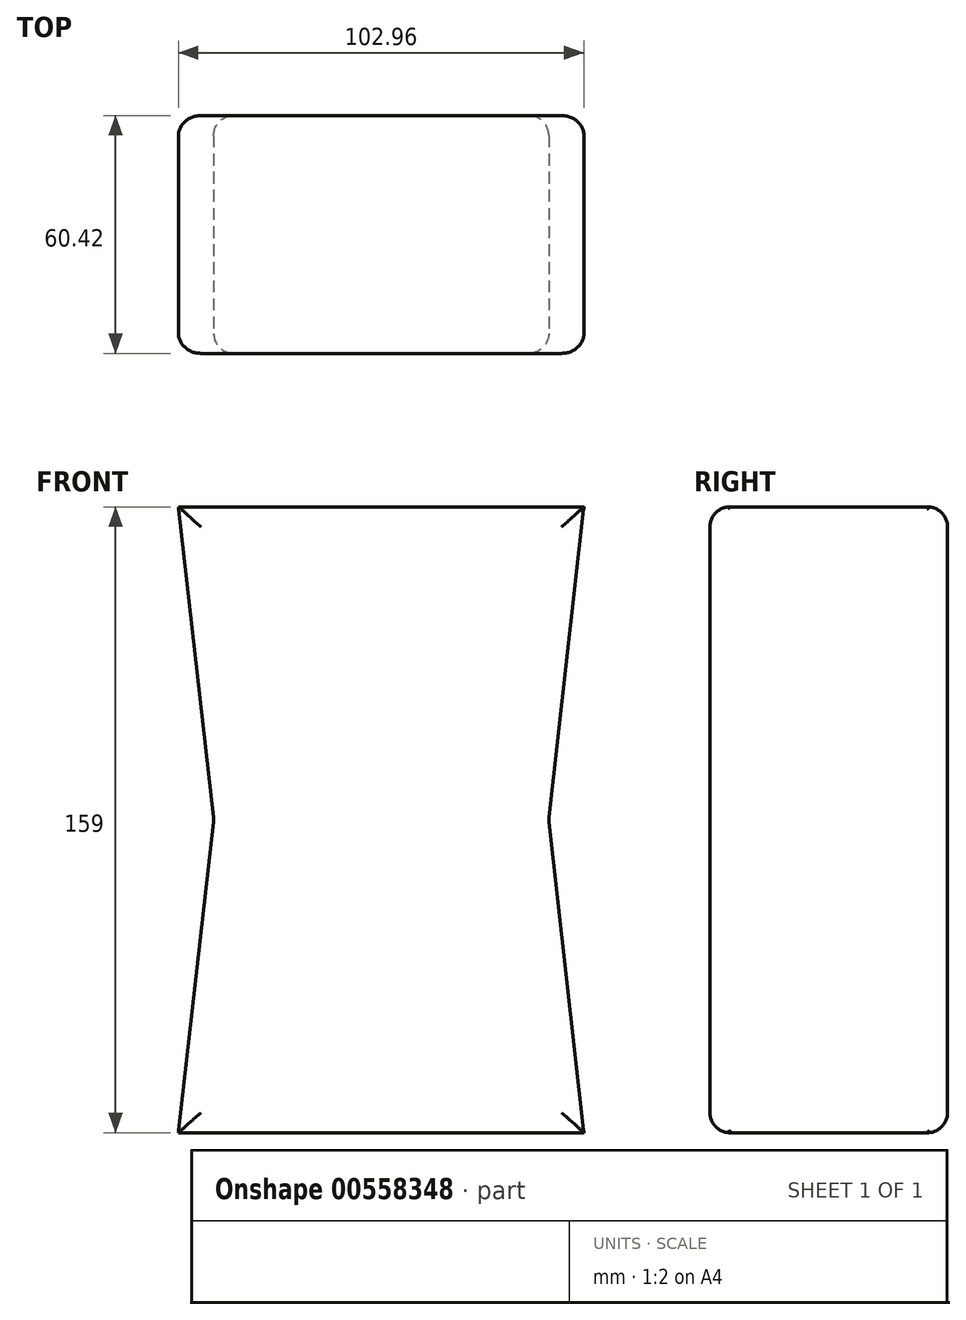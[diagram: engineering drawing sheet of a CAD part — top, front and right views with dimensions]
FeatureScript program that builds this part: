
annotation { "Feature Type Name" : "Feature", "Feature Type Description" : "" }
export const myFeature = defineFeature(function(context is Context, id is Id, definition is map)
    precondition{}
    {
        {
            var Q0;
            Q0=qCreatedBy(makeId("Top.planeOp"),FACE);
            var sketch = newSketch(context, id + "F0", { "sketchPlane" : qUnion([Q0])});
            skLineSegment(sketch, "E0.bottom", {"start": v(51.48, -30.2) * mm, "end": v(-51.48, -30.2) * mm});
            skLineSegment(sketch, "E0.top", {"start": v(51.48, 30.2) * mm, "end": v(-51.48, 30.2) * mm});
            skLineSegment(sketch, "E0.left", {"start": v(51.48, -30.2) * mm, "end": v(51.48, 30.2) * mm});
            skLineSegment(sketch, "E0.right", {"start": v(-51.48, -30.2) * mm, "end": v(-51.48, 30.2) * mm});
            skPoint(sketch, "E0.middle", {"position": v(0, 0) * mm});
            skSolve(sketch);
        }
        {
            var Q0;
            Q0 = qSketchRegion(id + "F0", true);
            extrude(context, id + "F1", {"entities" : qUnion([Q0]), "depth" : 0.25 * mm, "offsetDistance" : 25.4 * mm});
        }
        {
            var Q0;
            Q0=makeQuery(id+"F1.opExtrude","CAP_FACE",FACE,{"disambiguationData":[OSD([sQuery(id+"F0.wireOp",EDGE,"E0.bottom"),sQuery(id+"F0.wireOp",EDGE,"E0.top"),sQuery(id+"F0.wireOp",EDGE,"E0.left"),sQuery(id+"F0.wireOp",EDGE,"E0.right")])],"isStart":false});
            var sketch = newSketch(context, id + "F2", { "sketchPlane" : qUnion([Q0])});
            skLineSegment(sketch, "E1.bottom", {"start": v(42.54, -30.2) * mm, "end": v(-42.54, -30.2) * mm});
            skLineSegment(sketch, "E1.top", {"start": v(42.54, 30.2) * mm, "end": v(-42.54, 30.2) * mm});
            skLineSegment(sketch, "E1.left", {"start": v(42.54, -30.2) * mm, "end": v(42.54, 30.2) * mm});
            skLineSegment(sketch, "E1.right", {"start": v(-42.54, -30.2) * mm, "end": v(-42.54, 30.2) * mm});
            skPoint(sketch, "E1.middle", {"position": v(0, 0) * mm});
            skSolve(sketch);
        }
        {
            var Q0;
            Q0=makeQuery(id+"F2.imprint","IMPRINT",FACE,{"disambiguationData":[TD([[makeQuery(id+"F2.imprint","IMPRINT",EDGE,{"derivedFrom":sQuery(id+"F2.wireOp",EDGE,"E1.bottom")}),-1.0]])]});
            extrude(context, id + "F3", {"entities" : qUnion([Q0]), "operationType" : NewBodyOperationType.ADD, "depth" : 79.25 * mm, "offsetDistance" : 25.4 * mm});
        }
        {
            var Q1;
            {var subQ0=sQuery(id+"F0.wireOp",EDGE,"E0.top");var subQ1=sQuery(id+"F0.wireOp",EDGE,"E0.right");var subQ2=sQuery(id+"F0.wireOp",EDGE,"E0.bottom");Q1=makeQuery(id+"F3.boolean.opBoolean","SPLIT",FACE,{"disambiguationData":[TD([makeQuery(id+"F1.opExtrude","SWEPT_FACE",FACE,{"disambiguationData":[OSD([subQ1])]})])],"derivedFrom":makeQuery(id+"F1.opExtrude","CAP_FACE",FACE,{"disambiguationData":[OSD([subQ2,subQ0,sQuery(id+"F0.wireOp",EDGE,"E0.left"),subQ1])],"isStart":false})});}
            var Q2;
            Q2=makeQuery(id+"F3.opExtrude","CAP_FACE",FACE,{"disambiguationData":[OSD([sQuery(id+"F2.wireOp",EDGE,"E1.bottom"),sQuery(id+"F2.wireOp",EDGE,"E1.top"),sQuery(id+"F2.wireOp",EDGE,"E1.left"),sQuery(id+"F2.wireOp",EDGE,"E1.right")])],"isStart":false});
            loft(context, id + "F4", {"operationType" : NewBodyOperationType.ADD, "sheetProfilesArray" : [{ "sheetProfileEntities" : qUnion([Q1]) }, { "sheetProfileEntities" : qUnion([Q2]) }]});
        }
        {
            var Q1;
            {var subQ0=sQuery(id+"F0.wireOp",EDGE,"E0.left");var subQ1=sQuery(id+"F0.wireOp",EDGE,"E0.top");var subQ2=sQuery(id+"F0.wireOp",EDGE,"E0.bottom");Q1=makeQuery(id+"F3.boolean.opBoolean","SPLIT",FACE,{"disambiguationData":[TD([makeQuery(id+"F1.opExtrude","SWEPT_FACE",FACE,{"disambiguationData":[OSD([subQ0])]})])],"derivedFrom":makeQuery(id+"F1.opExtrude","CAP_FACE",FACE,{"disambiguationData":[OSD([subQ2,subQ1,subQ0,sQuery(id+"F0.wireOp",EDGE,"E0.right")])],"isStart":false})});}
            var Q2;
            Q2=makeQuery(id+"F3.opExtrude","CAP_FACE",FACE,{"disambiguationData":[OSD([sQuery(id+"F2.wireOp",EDGE,"E1.bottom"),sQuery(id+"F2.wireOp",EDGE,"E1.top"),sQuery(id+"F2.wireOp",EDGE,"E1.left"),sQuery(id+"F2.wireOp",EDGE,"E1.right")])],"isStart":false});
            loft(context, id + "F5", {"operationType" : NewBodyOperationType.ADD, "sheetProfilesArray" : [{ "sheetProfileEntities" : qUnion([Q1]) }, { "sheetProfileEntities" : qUnion([Q2]) }]});
        }
        {
            var Q0;
            Q0=makeQuery(id+"F1.opExtrude","SWEPT_BODY",BODY,{"disambiguationData":[OSD([sQuery(id+"F0.wireOp",EDGE,"E0.bottom"),sQuery(id+"F0.wireOp",EDGE,"E0.top"),sQuery(id+"F0.wireOp",EDGE,"E0.left"),sQuery(id+"F0.wireOp",EDGE,"E0.right")])]});
            var Q1;
            Q1=makeQuery(id+"F3.opExtrude","CAP_FACE",FACE,{"disambiguationData":[OSD([sQuery(id+"F2.wireOp",EDGE,"E1.bottom"),sQuery(id+"F2.wireOp",EDGE,"E1.top"),sQuery(id+"F2.wireOp",EDGE,"E1.left"),sQuery(id+"F2.wireOp",EDGE,"E1.right")])],"isStart":false});
            mirror(context, id + "F6", {"operationType" : NewBodyOperationType.ADD, "entities" : qUnion([Q0]), "mirrorPlane" : qUnion([Q1])});
        }
        {
            var Q0;
            Q0=makeQuery(id+"F6.opPattern","COPY",FACE,{"derivedFrom":makeQuery(id+"F4.opLoft","SWEPT_FACE",FACE,{"disambiguationData":[OSD([sQuery(id+"F0.wireOp",EDGE,"E0.bottom"),sQuery(id+"F0.wireOp",EDGE,"E0.top"),sQuery(id+"F0.wireOp",EDGE,"E0.right"),sQuery(id+"F2.wireOp",EDGE,"E1.bottom"),sQuery(id+"F2.wireOp",EDGE,"E1.top"),sQuery(id+"F2.wireOp",EDGE,"E1.right")])]}),"instanceName":"1"});
            var Q1;
            Q1=makeQuery(id+"F4.opLoft","SWEPT_FACE",FACE,{"disambiguationData":[OSD([sQuery(id+"F0.wireOp",EDGE,"E0.bottom"),sQuery(id+"F0.wireOp",EDGE,"E0.top"),sQuery(id+"F0.wireOp",EDGE,"E0.right"),sQuery(id+"F2.wireOp",EDGE,"E1.bottom"),sQuery(id+"F2.wireOp",EDGE,"E1.top"),sQuery(id+"F2.wireOp",EDGE,"E1.right")])]});
            var Q2;
            Q2=makeQuery(id+"F5.opLoft","SWEPT_FACE",FACE,{"disambiguationData":[OSD([sQuery(id+"F0.wireOp",EDGE,"E0.bottom"),sQuery(id+"F0.wireOp",EDGE,"E0.top"),sQuery(id+"F0.wireOp",EDGE,"E0.left"),sQuery(id+"F2.wireOp",EDGE,"E1.bottom"),sQuery(id+"F2.wireOp",EDGE,"E1.top"),sQuery(id+"F2.wireOp",EDGE,"E1.left")])]});
            var Q3;
            Q3=makeQuery(id+"F6.opPattern","COPY",FACE,{"derivedFrom":makeQuery(id+"F5.opLoft","SWEPT_FACE",FACE,{"disambiguationData":[OSD([sQuery(id+"F0.wireOp",EDGE,"E0.bottom"),sQuery(id+"F0.wireOp",EDGE,"E0.top"),sQuery(id+"F0.wireOp",EDGE,"E0.left"),sQuery(id+"F2.wireOp",EDGE,"E1.bottom"),sQuery(id+"F2.wireOp",EDGE,"E1.top"),sQuery(id+"F2.wireOp",EDGE,"E1.left")])]}),"instanceName":"1"});
            var Q4;
            Q4=makeQuery(id+"F1.opExtrude","CAP_EDGE",EDGE,{"disambiguationData":[OSD([sQuery(id+"F0.wireOp",EDGE,"E0.bottom")])],"isStart":true});
            var Q5;
            Q5=makeQuery(id+"F1.opExtrude","CAP_EDGE",EDGE,{"disambiguationData":[OSD([sQuery(id+"F0.wireOp",EDGE,"E0.top")])],"isStart":true});
            var Q6;
            Q6=makeQuery(id+"F6.opPattern","COPY",EDGE,{"derivedFrom":makeQuery(id+"F1.opExtrude","CAP_EDGE",EDGE,{"disambiguationData":[OSD([sQuery(id+"F0.wireOp",EDGE,"E0.top")])],"isStart":true}),"instanceName":"1"});
            var Q7;
            Q7=makeQuery(id+"F6.opPattern","COPY",EDGE,{"derivedFrom":makeQuery(id+"F1.opExtrude","CAP_EDGE",EDGE,{"disambiguationData":[OSD([sQuery(id+"F0.wireOp",EDGE,"E0.bottom")])],"isStart":true}),"instanceName":"1"});
            fillet(context, id + "F7", {"entities" : qUnion([Q0, Q1, Q2, Q3, Q4, Q5, Q6, Q7]), "radius" : 5.08 * mm, "tangentPropagation" : true, "allowEdgeOverflow" : false});
        }
    });
